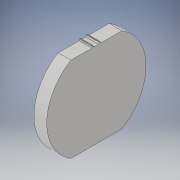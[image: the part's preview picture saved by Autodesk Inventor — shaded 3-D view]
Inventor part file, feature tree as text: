
AUTODESK INVENTOR PART (.ipt)
format: ipt  version: 2017 (Build 210142000, 142)  size: 128,000 bytes
history: native  units: in
note: dims shown in document units (in); Inventor stores cm internally (conversion verified against a paired STEP export)
features: extrude x1, sketch x1
ambient origin geometry x8: Origin, YZ Plane, XZ Plane, XY Plane, X Axis, Y Axis, Z Axis, Center Point
bodies: Body1 (feature_tree)
feature tree (2):
  extrude  "connection"  [1 undecoded]
  sketch  "Sketch1"  dims[d12=6.6667in d14=1.0in d15=0.0in d85=4.0in d86=0.5833in d87=3.8873in d88=3.8873in d89=1.7083in d90=0.0625in d91=0.0625in d92=1.6458in d93=0.25in d94=0.125in d95=0.0892in d96=0.0884in d97=45.0deg d98=3.3333in d99=0.125in]
note: 1 required parameter value undecoded (feature->parameter linkage not recoverable at this tier; creation-order binding heuristic only, values carry confidence <= 0.55)
